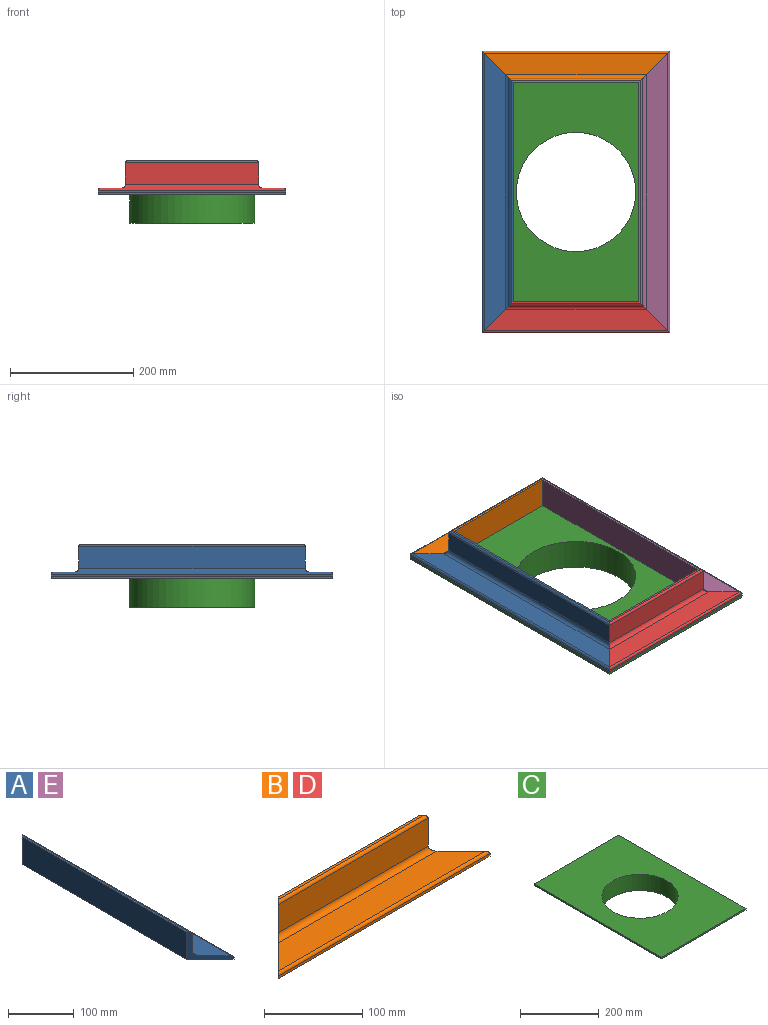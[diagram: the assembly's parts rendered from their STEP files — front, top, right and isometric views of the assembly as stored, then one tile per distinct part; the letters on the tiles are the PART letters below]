
ASSEMBLY  parts=5 mates=4
PART A: 11 faces, bbox 50.8x457.2x50.8 mm
  f0: plane 50.8x50.8mm, normal (-0.71,-0.71,0), area 861.5mm2, adj f2,f3,f4,f5,f6,f7,f8,f9
  f1: plane 50.8x50.8mm, normal (-0.71,0.71,0), area 861.5mm2, adj f2,f3,f4,f5,f6,f7,f8,f9
  f2: plane 368.3x34.93mm, normal (1,0,0), area 12862.9mm2, adj f0,f1,f3,f10
  f3: cylinder r=6.35mm len=381mm, axis (0,1,0), area 3719.7mm2, adj f0,f1,f2,f4
  f4: plane 450.85x34.93mm, normal (0,0,1), area 14526.2mm2, adj f0,f1,f3,f5
  f5: cylinder r=3.17mm len=457.2mm, axis (0,1,0), area 2268.7mm2, adj f0,f1,f4,f6
  f6: plane 457.2x3.18mm, normal (1,0,0), area 1451.6mm2, adj f0,f1,f5,f7
  f7: plane 457.2x50.8mm, normal (0,0,-1), area 20645.1mm2, adj f0,f1,f6,f8
  f8: plane 355.6x50.8mm, normal (-1,0,0), area 18064.5mm2, adj f0,f1,f7,f9
  f9: plane 361.95x3.18mm, normal (0,0,1), area 1139.1mm2, adj f0,f1,f8,f10
  f10: cylinder r=3.17mm len=368.3mm, axis (0,1,0), area 1825.3mm2, adj f0,f1,f2,f9
PART B: 11 faces, bbox 304.8x50.8x50.8 mm
  f0: plane 50.8x50.8mm, normal (-0.71,0.71,0), area 861.5mm2, adj f2,f3,f4,f5,f6,f7,f8,f9
  f1: plane 50.8x50.8mm, normal (0.71,0.71,0), area 861.5mm2, adj f2,f3,f4,f5,f6,f7,f8,f9
  f2: plane 215.9x34.93mm, normal (0,-1,0), area 7540.3mm2, adj f0,f1,f3,f10
  f3: cylinder r=6.35mm len=228.6mm, axis (1,0,0), area 2199.6mm2, adj f0,f1,f2,f4
  f4: plane 298.45x34.93mm, normal (0,0,1), area 9203.6mm2, adj f0,f1,f3,f5
  f5: cylinder r=3.17mm len=304.8mm, axis (1,0,0), area 1508.6mm2, adj f0,f1,f4,f6
  f6: plane 304.8x3.18mm, normal (0,-1,0), area 967.7mm2, adj f0,f1,f5,f7
  f7: plane 304.8x50.8mm, normal (0,0,-1), area 12903.2mm2, adj f0,f1,f6,f8
  f8: plane 203.2x50.8mm, normal (0,1,0), area 10322.6mm2, adj f0,f1,f7,f9
  f9: plane 209.55x3.18mm, normal (0,0,1), area 655.2mm2, adj f0,f1,f8,f10
  f10: cylinder r=3.17mm len=215.9mm, axis (1,0,0), area 1065.3mm2, adj f0,f1,f2,f9
PART C: 9 faces, bbox 304.8x457.2x50.8 mm
  f0: cylinder r=101.6mm len=203.2mm, axis (0,0,1), area 29389mm2, adj f1,f3
  f1: plane 457.2x304.8mm, normal (0,0,-1), area 106925.3mm2, adj f0,f4,f5,f6,f7
  f2: cylinder r=96.84mm len=193.68mm, axis (0,0,1), area 30909.2mm2, adj f3,f8
  f3: plane 203.2x203.2mm, normal (0,0,-1), area 2969mm2, adj f0,f2
  f4: plane 457.2x4.76mm, normal (-1,0,0), area 2177.4mm2, adj f1,f6,f7,f8
  f5: plane 457.2x4.76mm, normal (1,0,0), area 2177.4mm2, adj f1,f6,f7,f8
  f6: plane 304.8x4.76mm, normal (0,1,0), area 1451.6mm2, adj f1,f4,f5,f8
  f7: plane 304.8x4.76mm, normal (0,-1,0), area 1451.6mm2, adj f1,f4,f5,f8
  f8: plane 457.2x304.8mm, normal (0,0,1), area 109894.3mm2, adj f2,f4,f5,f6,f7
PART D: same geometry as B
PART E: same geometry as A
PLACE A rot(axis=(0,0,-1),180deg) t=(1766.05,-61.65,153.01)mm
PLACE B rot(axis=(0,0,1),180deg) t=(1766.05,-61.65,153.01)mm
PLACE C t=(242.05,-61.65,156.18)mm
PLACE D t=(242.05,-61.65,153.01)mm
PLACE E t=(242.05,-61.65,153.01)mm
MATE fastened A.f4 <-> B.f4  axis (0,0,1) through (872.29,146.32,1530.96)mm
MATE fastened E.f4 <-> D.f4  axis (0,0,1) through (1135.82,-269.61,1530.96)mm
MATE fastened B.f4 <-> E.f4  axis (0,0,1) through (1135.82,146.32,1530.96)mm
MATE fastened C.f8 <-> B.f7  axis (0,0,1) through (851.65,166.95,1524.61)mm
